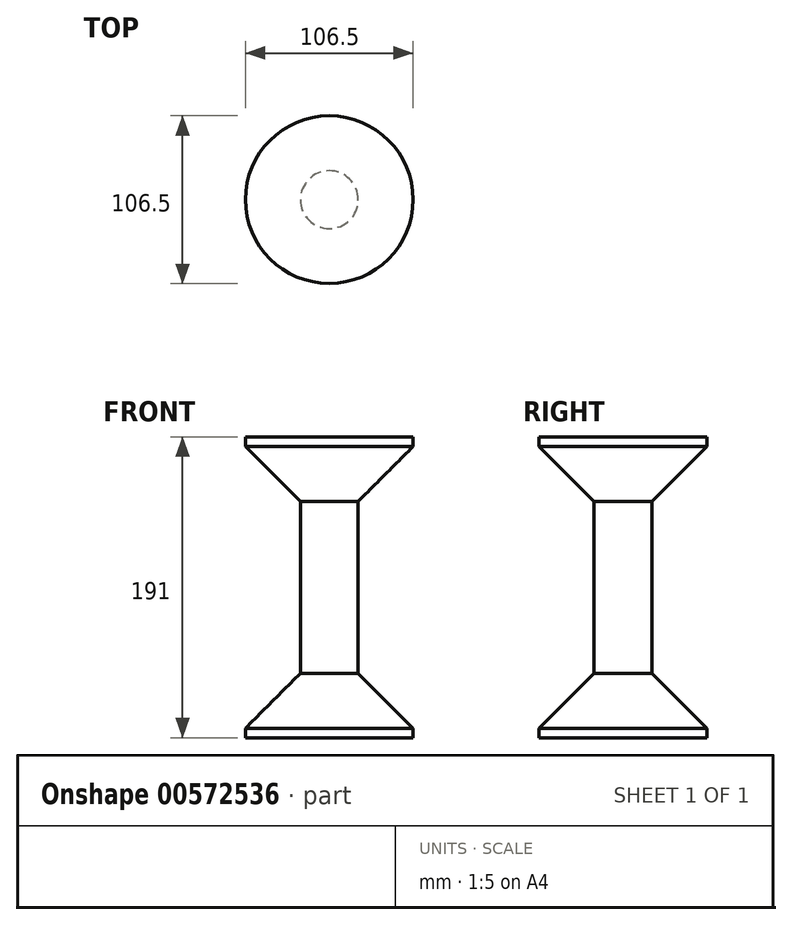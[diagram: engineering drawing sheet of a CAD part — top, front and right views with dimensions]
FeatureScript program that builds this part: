
annotation { "Feature Type Name" : "Feature", "Feature Type Description" : "" }
export const myFeature = defineFeature(function(context is Context, id is Id, definition is map)
    precondition{}
    {
        {
            var Q0;
            Q0=qCreatedBy(makeId("Top.planeOp"),FACE);
            var sketch = newSketch(context, id + "F0", { "sketchPlane" : qUnion([Q0])});
            skCircle(sketch, "E0", {"center": v(0, 0) * mm, "radius": 18.38 * mm});
            skSolve(sketch);
        }
        {
            var Q0;
            Q0=makeQuery(id+"F0.imprint","IMPRINT",FACE,{"disambiguationData":[TD([[makeQuery(id+"F0.imprint","IMPRINT",EDGE,{"derivedFrom":sQuery(id+"F0.wireOp",EDGE,"E0")}),1.0]])]});
            extrude(context, id + "F1", {"entities" : qUnion([Q0]), "depth" : 89.92 * mm, "offsetDistance" : 25.4 * mm});
        }
        {
            var Q0;
            Q0=makeQuery(id+"F1.opExtrude","CAP_FACE",FACE,{"disambiguationData":[OSD([sQuery(id+"F0.wireOp",EDGE,"E0")])],"isStart":false});
            var sketch = newSketch(context, id + "F2", { "sketchPlane" : qUnion([Q0])});
            skCircle(sketch, "E1", {"center": v(0, 0) * mm, "radius": 53.25 * mm});
            skSolve(sketch);
        }
        {
            var Q0;
            Q0=makeQuery(id+"F2.imprint","IMPRINT",FACE,{"disambiguationData":[TD([[makeQuery(id+"F2.imprint","IMPRINT",EDGE,{"derivedFrom":sQuery(id+"F2.wireOp",EDGE,"E1")}),1.0]])]});
            var Q1;
            Q1=makeQuery(id+"F2.imprint","IMPRINT",FACE,{"disambiguationData":[TD([[makeQuery(id+"F2.imprint","IMPRINT",EDGE,{"derivedFrom":makeQuery(id+"F1.opExtrude","CAP_EDGE",EDGE,{"disambiguationData":[OSD([sQuery(id+"F0.wireOp",EDGE,"E0")])],"isStart":false})}),1.0]])]});
            extrude(context, id + "F3", {"entities" : qUnion([Q0, Q1]), "operationType" : NewBodyOperationType.ADD, "depth" : 5.6 * mm, "offsetDistance" : 25.4 * mm});
        }
        {
            var Q0;
            Q0=makeQuery(id+"F1.opExtrude","SWEPT_BODY",BODY,{"disambiguationData":[OSD([sQuery(id+"F0.wireOp",EDGE,"E0")])]});
            var Q1;
            Q1=qCreatedBy(makeId("Top.planeOp"),FACE);
            mirror(context, id + "F4", {"operationType" : NewBodyOperationType.ADD, "entities" : qUnion([Q0]), "mirrorPlane" : qUnion([Q1])});
        }
        {
            var Q0;
            {var subQ0=makeQuery(id+"F1.opExtrude","SWEPT_FACE",FACE,{"disambiguationData":[OSD([sQuery(id+"F0.wireOp",EDGE,"E0")])]});Q0=makeQuery(id+"F4.boolean.opBoolean","MERGE",FACE,{"derivedFrom":[subQ0,makeQuery(id+"F4.opPattern","COPY",FACE,{"derivedFrom":subQ0,"instanceName":"1"})]});}
            chamfer(context, id + "F5", {"entities" : qUnion([Q0]), "width" : 35.3 * mm, "tangentPropagation" : true});
        }
    });
